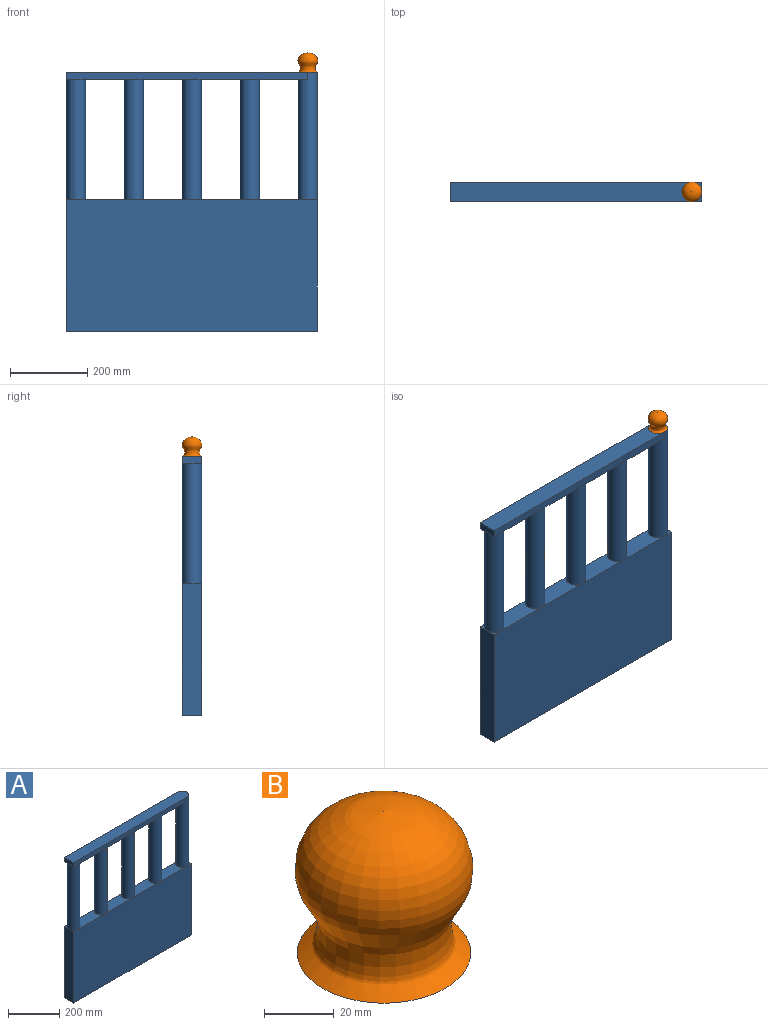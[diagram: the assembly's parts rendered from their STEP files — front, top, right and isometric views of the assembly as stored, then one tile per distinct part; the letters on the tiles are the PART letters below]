
ASSEMBLY  parts=2 mates=1
PART A: 28 faces, bbox 650x50x670 mm
  f0: plane 650x50mm, normal (0,0,1), area 32231.7mm2, adj f14,f25,f26,f27
  f1: plane 25x25mm, normal (0,0,1), area 134.1mm2, adj f8,f13,f18
  f2: plane 25x25mm, normal (0,0,1), area 134.1mm2, adj f8,f12,f18
  f3: plane 150x50mm, normal (0,0,1), area 5536.5mm2, adj f12,f13,f17,f18
  f4: plane 150x50mm, normal (0,0,1), area 5536.5mm2, adj f12,f13,f16,f17
  f5: plane 150x50mm, normal (0,0,1), area 5536.5mm2, adj f12,f13,f15,f16
  f6: plane 25x25mm, normal (0,0,1), area 134.1mm2, adj f10,f13,f14
  f7: plane 150x50mm, normal (0,0,1), area 5536.5mm2, adj f12,f13,f14,f15
  f8: plane 340x50mm, normal (-1,0,0), area 17000mm2, adj f1,f2,f9,f12,f13
  f9: plane 650x50mm, normal (0,0,-1), area 32500mm2, adj f8,f10,f12,f13
  f10: plane 340x50mm, normal (1,0,0), area 17000mm2, adj f6,f9,f11,f12,f13
  f11: plane 25x25mm, normal (0,0,1), area 134.1mm2, adj f10,f12,f14
  f12: plane 650x340mm, normal (0,-1,0), area 221000mm2, adj f2,f3,f4,f5,f7,f8,f9,f10
  f13: plane 650x340mm, normal (0,1,0), area 221000mm2, adj f1,f3,f4,f5,f6,f7,f8,f9
  f14: cylinder r=25mm len=330mm, axis (0,0,-1), area 50265.5mm2, adj f0,f6,f7,f11,f19,f25,f27
  f15: cylinder r=25mm len=310mm, axis (0,0,-1), area 48694.7mm2, adj f5,f7,f19,f20
  f16: cylinder r=25mm len=310mm, axis (0,0,-1), area 48694.7mm2, adj f4,f5,f20,f21
  f17: cylinder r=25mm len=310mm, axis (0,0,-1), area 48694.7mm2, adj f3,f4,f21,f22
  f18: cylinder r=25mm len=310mm, axis (0,0,-1), area 48694.7mm2, adj f1,f2,f3,f22,f23,f24
  f19: plane 150x50mm, normal (0,0,-1), area 5536.5mm2, adj f14,f15,f25,f27
  f20: plane 150x50mm, normal (0,0,-1), area 5536.5mm2, adj f15,f16,f25,f27
  f21: plane 150x50mm, normal (0,0,-1), area 5536.5mm2, adj f16,f17,f25,f27
  f22: plane 150x50mm, normal (0,0,-1), area 5536.5mm2, adj f17,f18,f25,f27
  f23: plane 25x25mm, normal (0,0,-1), area 134.1mm2, adj f18,f25,f26
  f24: plane 25x25mm, normal (0,0,-1), area 134.1mm2, adj f18,f26,f27
  f25: plane 625x20mm, normal (0,1,0), area 12500mm2, adj f0,f14,f19,f20,f21,f22,f23,f26
  f26: plane 50x20mm, normal (-1,0,0), area 1000mm2, adj f0,f23,f24,f25,f27
  f27: plane 625x20mm, normal (0,-1,0), area 12500mm2, adj f0,f14,f19,f20,f21,f22,f24,f26
PART B: 2 faces, bbox 51.2x51.2x50 mm
  f0: plane 50x50mm, normal (0,0,-1), area 1963.5mm2, adj f1
  f1: revolved ~51.19x51.19mm, area 8207.8mm2, adj f0
PLACE A t=(-68.18,-52.93,-45.34)mm
PLACE B t=(231.82,-77.93,189.66)mm
MATE fastened B.f0 <-> A.f14  axis (0,0,-1) through (231.82,-77.93,189.66)mm
